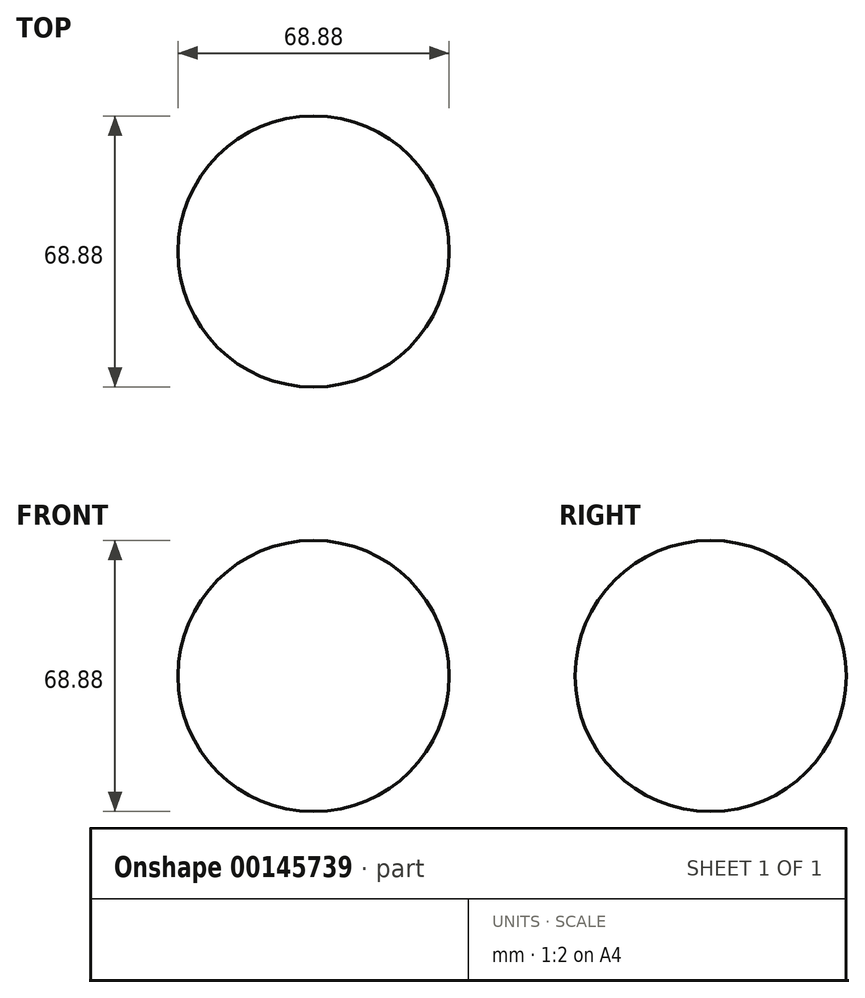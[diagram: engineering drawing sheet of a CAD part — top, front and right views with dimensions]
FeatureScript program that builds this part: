
annotation { "Feature Type Name" : "Feature", "Feature Type Description" : "" }
export const myFeature = defineFeature(function(context is Context, id is Id, definition is map)
    precondition{}
    {
        {
            var Q0;
            Q0=qCreatedBy(makeId("Front.planeOp"),FACE);
            var sketch = newSketch(context, id + "F0", { "sketchPlane" : qUnion([Q0])});
            skArc(sketch, "E0", {"start": v(0, -34.44) * mm, "mid": v(34.44, 0) * mm, "end": v(0, 34.44) * mm});
            skLineSegment(sketch, "E1", {"start": v(0, 34.44) * mm, "end": v(0, -34.44) * mm});
            skSolve(sketch);
        }
        {
            var Q0;
            Q0 = qSketchRegion(id + "F0", true);
            var Q1;
            Q1=sQuery(id+"F0.wireOp",EDGE,"E1");
            revolve(context, id + "F1", {"entities" : qUnion([Q0]), "axis" : qUnion([Q1]), "revolveType" : RevolveType.FULL});
        }
    });
